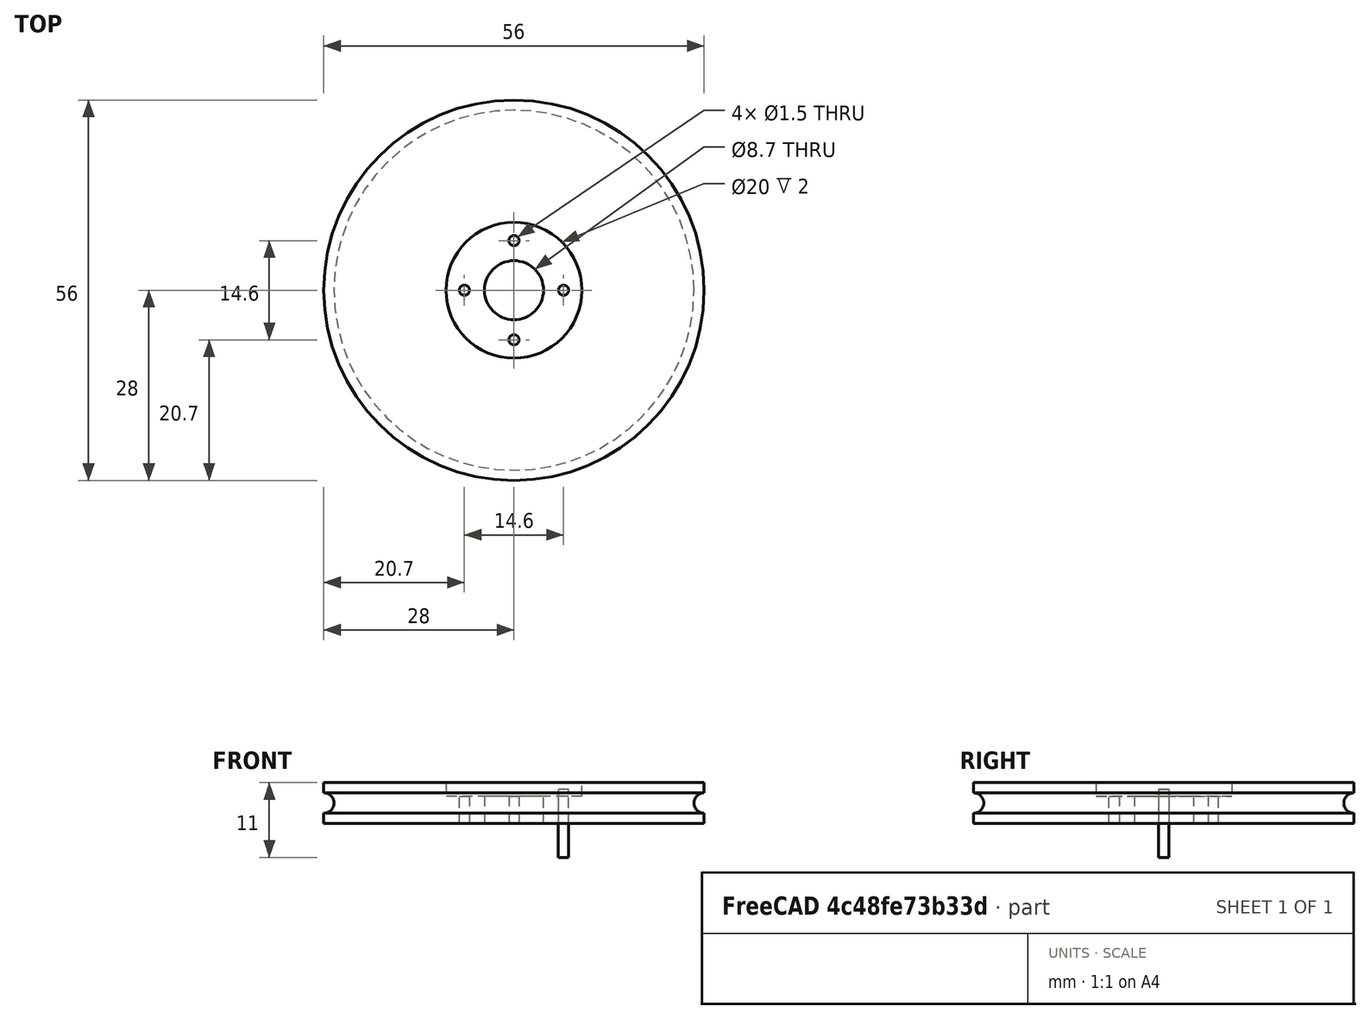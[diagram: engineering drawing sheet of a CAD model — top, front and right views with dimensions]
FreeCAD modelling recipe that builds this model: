
FCSTD DOCUMENT  (FreeCAD 0.21R33694 (Git))
Label: OJT1_T15P01_serve
License: All rights reserved
LicenseURL: http://en.wikipedia.org/wiki/All_rights_reserved
objects: Part::Cylinder×4, Part::Cut×4, Part::Torus×1, Part::FeaturePython×1
note: 9 computed .brp shape members not serialized (recipe doc carries the construction recipe); baked Part::Feature solids carry a one-line shape summary decoded from their .brp

FEATURE [Part::Cylinder] Cylinder
  Angle = 360
  AttacherType = Attacher::AttachEngine3D
  FirstAngle = 0
  Height = 6
  Radius = 28
  SecondAngle = 0
FEATURE [Part::Torus] Torus
  Angle1 = -180
  Angle2 = 180
  Angle3 = 360
  AttacherType = Attacher::AttachEngine3D
  Placement = pos=(0,0,3) rot=(0,0,1;0rad)
  Radius1 = 28
  Radius2 = 1.5
FEATURE [Part::Cut] Cut  label="roda_basica"
  Base = -> Cylinder
  Refine = true
  Tool = -> Torus
FEATURE [Part::Cylinder] Cylinder001  label="corona_serve"
  Angle = 360
  AttacherType = Attacher::AttachEngine3D
  FirstAngle = 0
  Height = 10
  Placement = pos=(0,0,4) rot=(0,0,1;0rad)
  Radius = 10
  SecondAngle = 0
FEATURE [Part::Cut] Cut001  label="roda_amb_forat_corona"
  Base = -> Cut
  Refine = true
  Tool = -> Cylinder001
FEATURE [Part::Cylinder] Cylinder002
  Angle = 360
  AttacherType = Attacher::AttachEngine3D
  FirstAngle = 0
  Height = 10
  Placement = pos=(0,0,-4) rot=(0,0,1;0rad)
  Radius = 4.35
  SecondAngle = 0
FEATURE [Part::Cut] Cut002  label="rueda_corona"
  Base = -> Cut001
  Refine = true
  Tool = -> Cylinder002
FEATURE [Part::Cylinder] Cylinder003
  Angle = 360
  AttacherType = Attacher::AttachEngine3D
  FirstAngle = 0
  Height = 10
  Placement = pos=(7.3,0,-5) rot=(0,0,1;0rad)
  Radius = 0.75
  SecondAngle = 0
FEATURE [Part::FeaturePython] Array  # Draft array (typed FeaturePython)
  AlwaysSyncPlacement = false
  Angle = 360
  ArrayType = 1
  Axis = (0,0,1)
  Base = -> Cylinder003
  Center = (0,0,0)
  Count = 4
  ExpandArray = false
  Fuse = false
  IntervalAxis = (0,0,0)
  IntervalX = (50,0,0)
  IntervalY = (0,50,0)
  IntervalZ = (0,0,50)
  NumberCircles = 3
  NumberPolar = 4
  NumberX = 2
  NumberY = 2
  NumberZ = 1
  PlacementList = 4 placements: [(7.3,0,-5),(0,7.3,-5),(-7.3,8.93992e-16,-5),(-1.62093e-15,-7.3,-5)]
  RadialDistance = 50
  ScaleList = (4) [(1,1,1),(1,1,1),(1,1,1),(1,1,1)]
  Symmetry = 1
  TangentialDistance = 25
FEATURE [Part::Cut] Cut003
  Base = -> Cut002
  Refine = true
  Tool = -> Array
